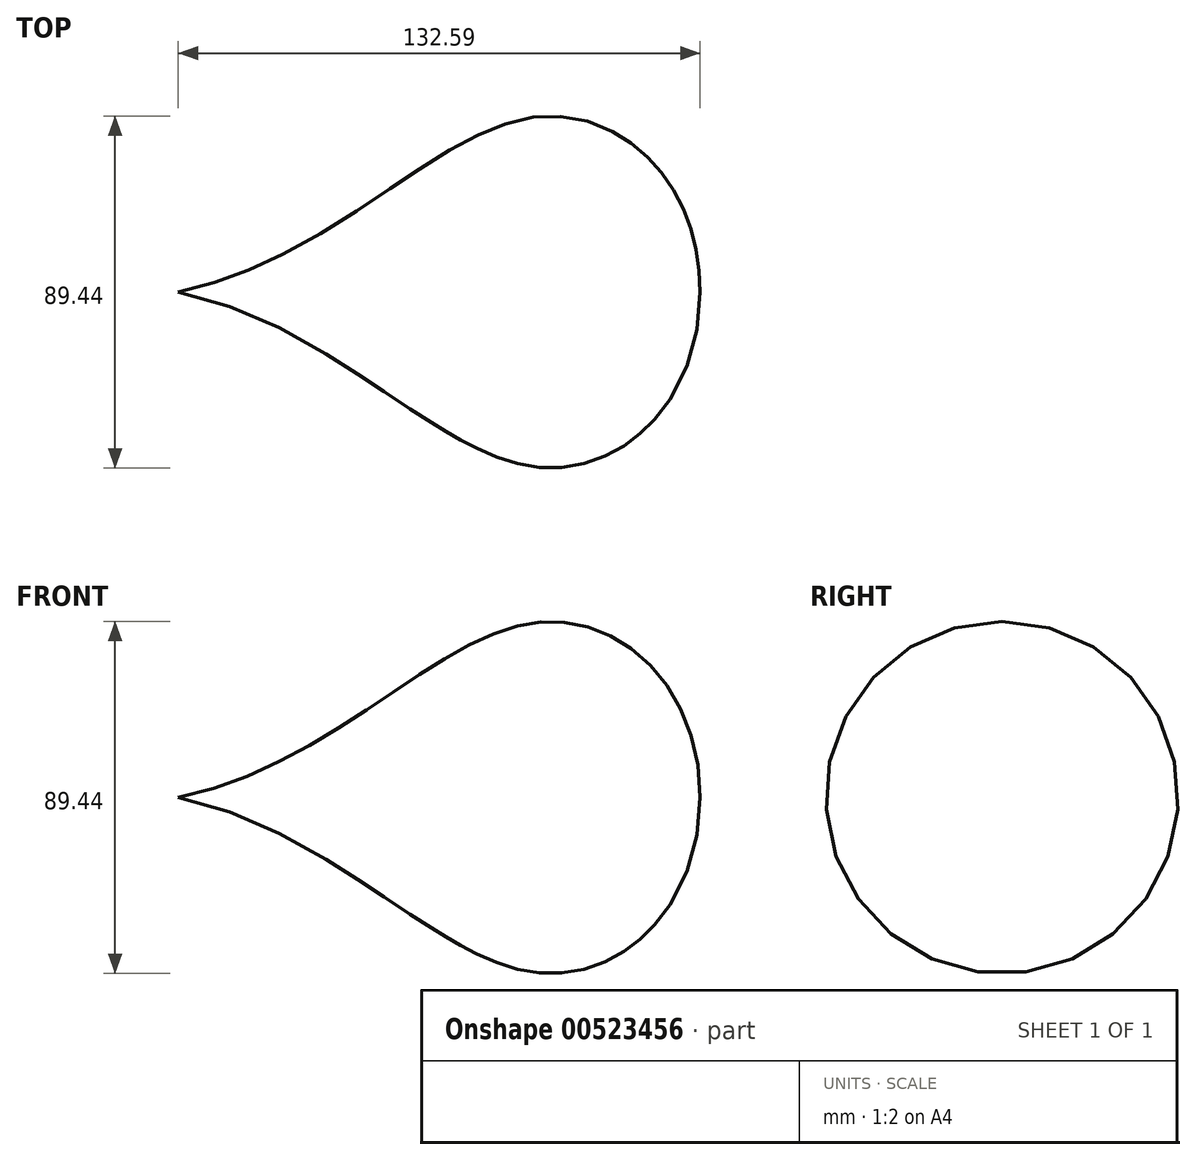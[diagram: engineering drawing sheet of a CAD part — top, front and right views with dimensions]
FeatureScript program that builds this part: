
annotation { "Feature Type Name" : "Feature", "Feature Type Description" : "" }
export const myFeature = defineFeature(function(context is Context, id is Id, definition is map)
    precondition{}
    {
        {
            var Q0;
            Q0=qCreatedBy(makeId("Front.planeOp"),FACE);
            var sketch = newSketch(context, id + "F0", { "sketchPlane" : qUnion([Q0])});
            skFitSpline(sketch, "E0", {"points": [v(0, 0) * mm, v(92.36, 44.63) * mm, v(132.6, 0) * mm], "startDerivative": vector(212.58, 43.2) * mm, "endDerivative": vector(0, -196.98) * mm});
            skLineSegment(sketch, "E1", {"start": v(0, 0) * mm, "end": v(132.6, 0) * mm});
            skSolve(sketch);
        }
        {
            var Q0;
            Q0=makeQuery(id+"F0.imprint","IMPRINT",FACE,{"disambiguationData":[TD([[makeQuery(id+"F0.imprint","IMPRINT",EDGE,{"derivedFrom":sQuery(id+"F0.wireOp",EDGE,"E0")}),-1.0]])]});
            var Q1;
            Q1=sQuery(id+"F0.wireOp",EDGE,"E1");
            revolve(context, id + "F1", {"entities" : qUnion([Q0]), "axis" : qUnion([Q1]), "revolveType" : RevolveType.FULL});
        }
    });
